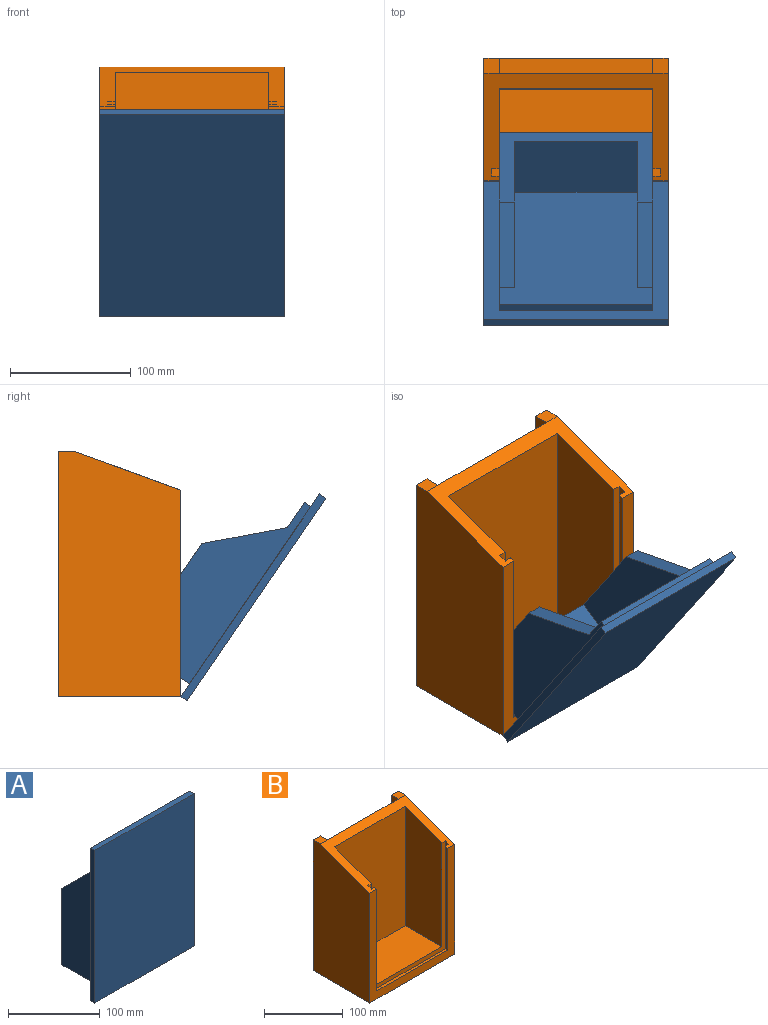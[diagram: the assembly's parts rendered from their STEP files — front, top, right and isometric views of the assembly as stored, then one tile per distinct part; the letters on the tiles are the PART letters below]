
ASSEMBLY  parts=2 mates=1
PART A: 17 faces, bbox 152.4x63.5x203.2 mm
  f0: plane 177.8x57.15mm, normal (1,0,0), area 7580.6mm2, adj f1,f2,f3,f8,f10,f11
  f1: plane 127x101.6mm, normal (0,1,0), area 3871mm2, adj f0,f3,f4,f5,f6,f7,f8,f9
  f2: plane 165.1x127mm, normal (0,1,0), area 17419.3mm2, adj f0,f4,f5,f6,f7,f8,f9,f10
  f3: plane 127x57.15mm, normal (0,0,-1), area 7258.1mm2, adj f0,f1,f4,f11
  f4: plane 177.8x57.15mm, normal (-1,0,0), area 7580.6mm2, adj f1,f2,f3,f9,f10,f11
  f5: plane 139.7x50.8mm, normal (1,0,0), area 5806.4mm2, adj f1,f2,f6,f9
  f6: plane 101.6x50.8mm, normal (0,0,1), area 5161.3mm2, adj f1,f2,f5,f7
  f7: plane 139.7x50.8mm, normal (-1,0,0), area 5806.4mm2, adj f1,f2,f6,f8
  f8: plane 50.8x50.8mm, normal (0,0.71,0.71), area 912.4mm2, adj f0,f1,f2,f7
  f9: plane 50.8x50.8mm, normal (0,0.71,0.71), area 912.4mm2, adj f1,f2,f4,f5
  f10: plane 127x6.35mm, normal (0,0,1), area 806.5mm2, adj f0,f2,f4,f11
  f11: plane 203.2x152.4mm, normal (0,1,0), area 8387.1mm2, adj f0,f3,f4,f10,f13,f14,f15,f16
  f12: plane 203.2x152.4mm, normal (0,-1,0), area 30967.7mm2, adj f13,f14,f15,f16
  f13: plane 152.4x6.35mm, normal (0,0,1), area 967.7mm2, adj f11,f12,f14,f16
  f14: plane 203.2x6.35mm, normal (1,0,0), area 1290.3mm2, adj f11,f12,f13,f15
  f15: plane 152.4x6.35mm, normal (0,0,-1), area 967.7mm2, adj f11,f12,f14,f16
  f16: plane 203.2x6.35mm, normal (-1,0,0), area 1290.3mm2, adj f11,f12,f13,f15
PART B: 24 faces, bbox 152.4x101.6x203.2 mm
  f0: plane 152.4x88.9mm, normal (0,-0.34,0.94), area 4033.6mm2, adj f2,f3,f4,f5,f7,f8,f10,f11
  f1: plane 127x3.94mm, normal (0,0,1), area 499.9mm2, adj f2,f3,f4,f14
  f2: plane 159.58x3.94mm, normal (-1,0,0), area 625.3mm2, adj f0,f1,f4,f14
  f3: plane 159.58x3.94mm, normal (1,0,0), area 625.3mm2, adj f0,f1,f4,f14
  f4: plane 170.84x152.4mm, normal (0,-1,0), area 5952.3mm2, adj f0,f1,f2,f3,f5,f6,f7
  f5: plane 203.2x101.6mm, normal (-1,0,0), area 19206.9mm2, adj f0,f4,f6,f20,f23
  f6: plane 152.4x101.6mm, normal (0,0,-1), area 15483.8mm2, adj f4,f5,f7,f23
  f7: plane 203.2x101.6mm, normal (1,0,0), area 19206.9mm2, adj f0,f4,f6,f19,f23
  f8: plane 190.5x127mm, normal (0,1,0), area 24193.5mm2, adj f0,f18,f21,f22
  f9: plane 127x65.91mm, normal (0,0,1), area 8371mm2, adj f10,f11,f12,f16
  f10: plane 185.88x127mm, normal (0,-1,0), area 23606.5mm2, adj f0,f9,f11,f12
  f11: plane 185.88x65.91mm, normal (-1,0,0), area 11461.2mm2, adj f0,f9,f10,f16
  f12: plane 185.88x65.91mm, normal (1,0,0), area 11461.2mm2, adj f0,f9,f10,f16
  f13: plane 168.24x6.35mm, normal (1,0,0), area 1061mm2, adj f0,f14,f16,f17
  f14: plane 165.93x139.7mm, normal (0,1,0), area 2913.7mm2, adj f0,f1,f2,f3,f13,f15,f17
  f15: plane 168.24x6.35mm, normal (-1,0,0), area 1061mm2, adj f0,f14,f16,f17
  f16: plane 168.24x139.7mm, normal (0,-1,0), area 2943.1mm2, adj f0,f9,f11,f12,f13,f15,f17
  f17: plane 139.7x6.35mm, normal (0,0,1), area 887.1mm2, adj f13,f14,f15,f16
  f18: plane 190.5x12.7mm, normal (-1,0,0), area 2419.3mm2, adj f8,f19,f22,f23
  f19: plane 12.7x12.7mm, normal (0,0,1), area 161.3mm2, adj f0,f7,f18,f23
  f20: plane 12.7x12.7mm, normal (0,0,1), area 161.3mm2, adj f0,f5,f21,f23
  f21: plane 190.5x12.7mm, normal (1,0,0), area 2419.3mm2, adj f8,f20,f22,f23
  f22: plane 127x12.7mm, normal (0,0,1), area 1612.9mm2, adj f8,f18,f21,f23
  f23: plane 203.2x152.4mm, normal (0,1,0), area 6774.2mm2, adj f5,f6,f7,f18,f19,f20,f21,f22
PLACE A rot(axis=(1,0,0),34.4deg) t=(-285.31,-105.05,-95.18)mm
PLACE B t=(-285.31,-21.39,-98.77)mm fixed
MATE planar B.f7 <-> A.f14  axis (1,0,0) through (-209.11,-57.9,-3.97)mm
